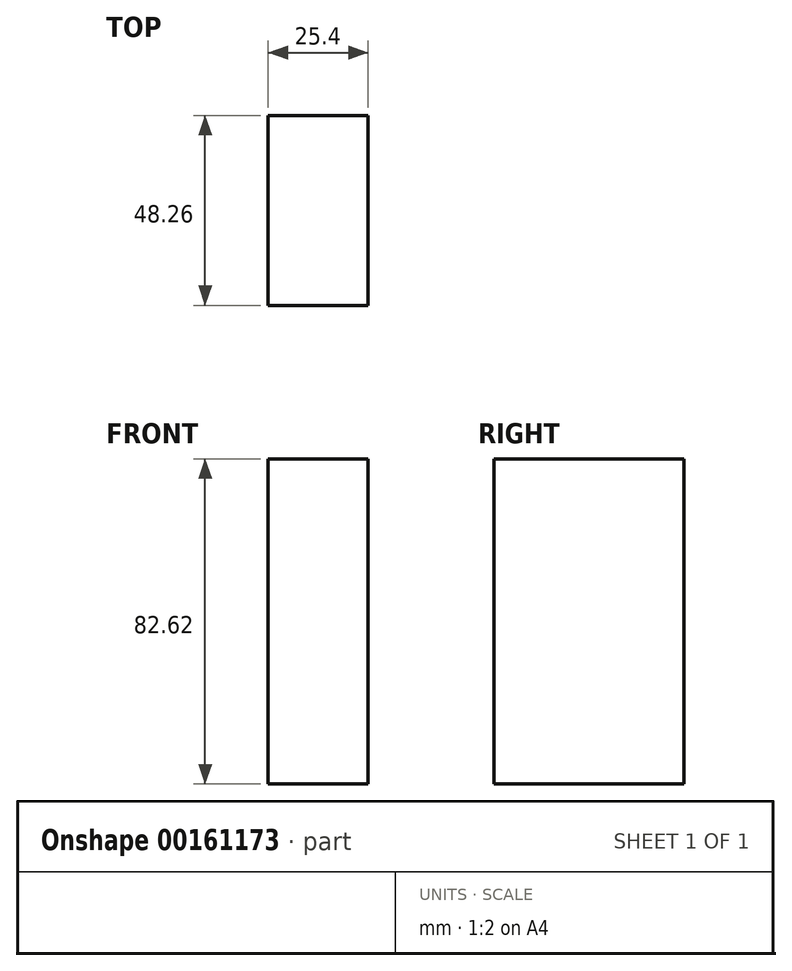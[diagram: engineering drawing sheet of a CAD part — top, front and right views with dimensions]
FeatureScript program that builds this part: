
annotation { "Feature Type Name" : "Feature", "Feature Type Description" : "" }
export const myFeature = defineFeature(function(context is Context, id is Id, definition is map)
    precondition{}
    {
        {
            var Q0;
            Q0=qCreatedBy(makeId("Right.planeOp"),FACE);
            var sketch = newSketch(context, id + "F0", { "sketchPlane" : qUnion([Q0])});
            skLineSegment(sketch, "E0.bottom", {"start": v(24.13, 41.31) * mm, "end": v(-24.13, 41.31) * mm});
            skLineSegment(sketch, "E0.top", {"start": v(24.13, -41.31) * mm, "end": v(-24.13, -41.31) * mm});
            skLineSegment(sketch, "E0.left", {"start": v(24.13, 41.31) * mm, "end": v(24.13, -41.31) * mm});
            skLineSegment(sketch, "E0.right", {"start": v(-24.13, 41.31) * mm, "end": v(-24.13, -41.31) * mm});
            skPoint(sketch, "E0.middle", {"position": v(0, 0) * mm});
            skSolve(sketch);
        }
        {
            var Q0;
            Q0=makeQuery(id+"F0.imprint","IMPRINT",FACE,{"disambiguationData":[TD([[makeQuery(id+"F0.imprint","IMPRINT",EDGE,{"derivedFrom":sQuery(id+"F0.wireOp",EDGE,"E0.bottom")}),1.0]])]});
            extrude(context, id + "F1", {"entities" : qUnion([Q0]), "endBound" : BoundingType.SYMMETRIC, "depth" : 25.4 * mm});
        }
    });
